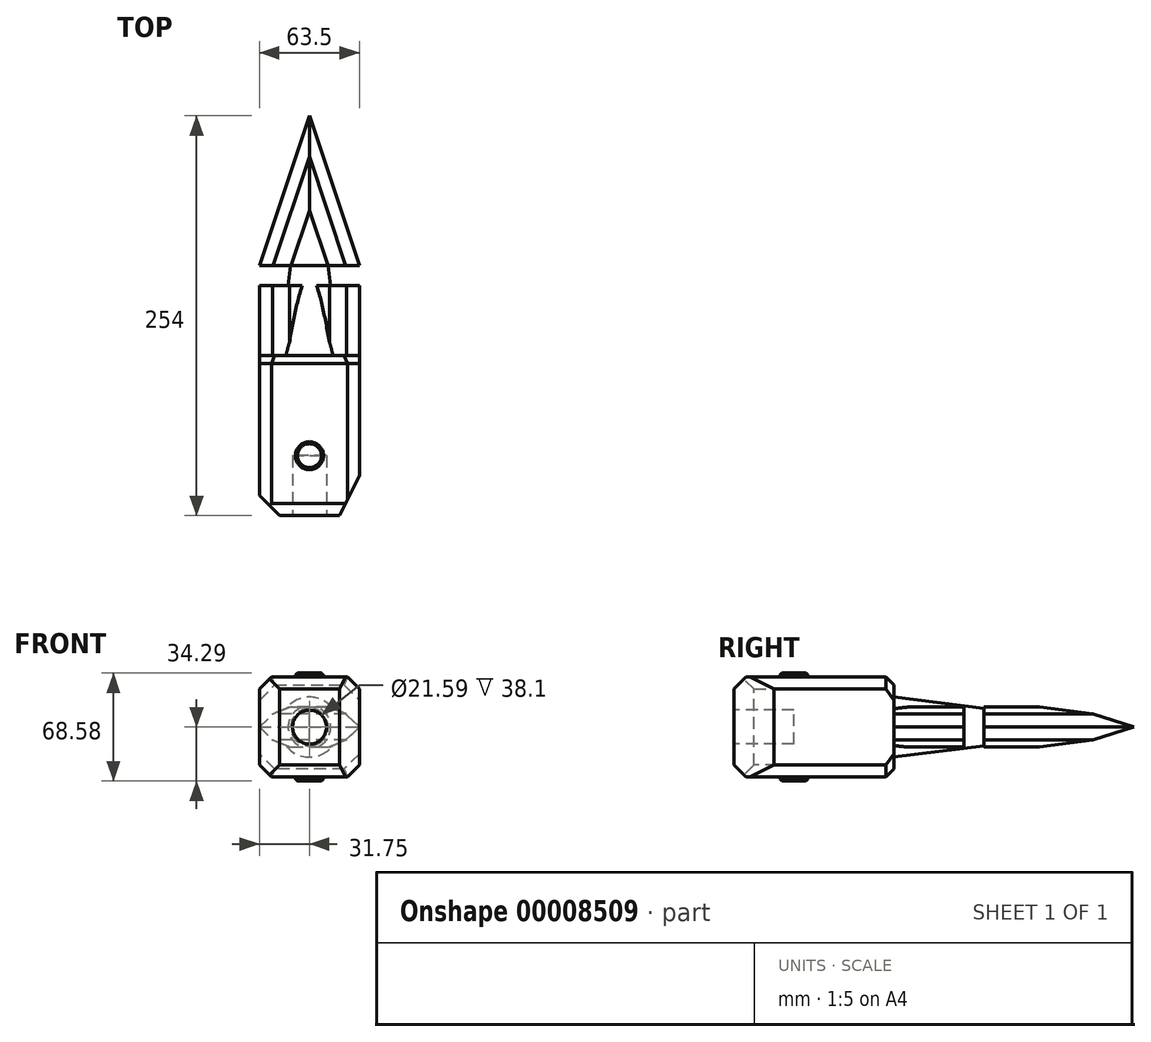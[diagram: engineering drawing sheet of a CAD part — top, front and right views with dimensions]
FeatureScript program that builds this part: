
annotation { "Feature Type Name" : "Feature", "Feature Type Description" : "" }
export const myFeature = defineFeature(function(context is Context, id is Id, definition is map)
    precondition{}
    {
        {
            var Q0;
            Q0=qCreatedBy(makeId("Top.planeOp"),FACE);
            var sketch = newSketch(context, id + "F0", { "sketchPlane" : qUnion([Q0])});
            skLineSegment(sketch, "E0.bottom", {"start": v(-31.75, -50.8) * mm, "end": v(31.75, -50.8) * mm});
            skLineSegment(sketch, "E0.top", {"start": v(-31.75, 50.8) * mm, "end": v(31.75, 50.8) * mm});
            skLineSegment(sketch, "E0.left", {"start": v(-31.75, -50.8) * mm, "end": v(-31.75, 50.8) * mm});
            skLineSegment(sketch, "E0.right", {"start": v(31.75, -50.8) * mm, "end": v(31.75, 50.8) * mm});
            skSolve(sketch);
        }
        {
            var Q0;
            Q0=makeQuery(id+"F0.imprint","IMPRINT",FACE,{"disambiguationData":[TD([[makeQuery(id+"F0.imprint","IMPRINT",EDGE,{"derivedFrom":sQuery(id+"F0.wireOp",EDGE,"E0.bottom")}),1.0]])]});
            extrude(context, id + "F1", {"entities" : qUnion([Q0]), "depth" : 63.5 * mm});
        }
        {
            var Q0;
            Q0=makeQuery(id+"F1.opExtrude","SWEPT_FACE",FACE,{"disambiguationData":[OSD([sQuery(id+"F0.wireOp",EDGE,"E0.bottom")])]});
            var sketch = newSketch(context, id + "F2", { "sketchPlane" : qUnion([Q0])});
            skLineSegment(sketch, "E1", {"start": v(0, 0) * mm, "end": v(0, 63.5) * mm, "construction": true});
            skLineSegment(sketch, "E2", {"start": v(-31.75, 31.75) * mm, "end": v(31.75, 31.75) * mm, "construction": true});
            skCircle(sketch, "E3", {"center": v(0, 31.75) * mm, "radius": 10.8 * mm});
            skSolve(sketch);
        }
        {
            var Q0;
            Q0=makeQuery(id+"F2.imprint","IMPRINT",FACE,{"disambiguationData":[TD([[makeQuery(id+"F2.imprint","IMPRINT",EDGE,{"derivedFrom":sQuery(id+"F2.wireOp",EDGE,"E3")}),1.0]])]});
            extrude(context, id + "F3", {"entities" : qUnion([Q0]), "operationType" : NewBodyOperationType.REMOVE, "oppositeDirection" : true, "depth" : 38.1 * mm});
        }
        {
            var Q0;
            Q0=makeQuery(id+"F1.opExtrude","CAP_FACE",FACE,{"disambiguationData":[OSD([sQuery(id+"F0.wireOp",EDGE,"E0.bottom"),sQuery(id+"F0.wireOp",EDGE,"E0.top"),sQuery(id+"F0.wireOp",EDGE,"E0.left"),sQuery(id+"F0.wireOp",EDGE,"E0.right")])],"isStart":false});
            var sketch = newSketch(context, id + "F4", { "sketchPlane" : qUnion([Q0])});
            skLineSegment(sketch, "E4.bottom", {"start": v(-31.75, -50.8) * mm, "end": v(-19.05, -50.8) * mm});
            skLineSegment(sketch, "E4.top", {"start": v(-31.75, -38.1) * mm, "end": v(-19.05, -38.1) * mm});
            skLineSegment(sketch, "E4.left", {"start": v(-31.75, -50.8) * mm, "end": v(-31.75, -38.1) * mm});
            skLineSegment(sketch, "E4.right", {"start": v(-19.05, -50.8) * mm, "end": v(-19.05, -38.1) * mm});
            skLineSegment(sketch, "E5.bottom", {"start": v(31.75, -50.8) * mm, "end": v(19.05, -50.8) * mm});
            skLineSegment(sketch, "E5.top", {"start": v(31.75, -25.4) * mm, "end": v(19.05, -25.4) * mm});
            skLineSegment(sketch, "E5.left", {"start": v(31.75, -50.8) * mm, "end": v(31.75, -25.4) * mm});
            skLineSegment(sketch, "E5.right", {"start": v(19.05, -50.8) * mm, "end": v(19.05, -25.4) * mm});
            skLineSegment(sketch, "E6", {"start": v(-31.75, -38.1) * mm, "end": v(-19.05, -50.8) * mm});
            skLineSegment(sketch, "E7", {"start": v(19.05, -50.8) * mm, "end": v(31.75, -25.4) * mm});
            skSolve(sketch);
        }
        {
            var Q0;
            Q0=makeQuery(id+"F4.imprint","IMPRINT",FACE,{"disambiguationData":[TD([[makeQuery(id+"F4.imprint","IMPRINT",EDGE,{"derivedFrom":sQuery(id+"F4.wireOp",EDGE,"E4.bottom")}),1.0]])]});
            var Q1;
            Q1=makeQuery(id+"F4.imprint","IMPRINT",FACE,{"disambiguationData":[TD([[makeQuery(id+"F4.imprint","IMPRINT",EDGE,{"derivedFrom":sQuery(id+"F4.wireOp",EDGE,"E5.bottom")}),1.0]])]});
            extrude(context, id + "F5", {"entities" : qUnion([Q0, Q1]), "operationType" : NewBodyOperationType.REMOVE, "oppositeDirection" : true, "depth" : 63.5 * mm});
        }
        {
            var Q0;
            Q0=makeQuery(id+"F1.opExtrude","CAP_EDGE",EDGE,{"disambiguationData":[OSD([sQuery(id+"F0.wireOp",EDGE,"E0.left")])],"isStart":false});
            var Q1;
            Q1=makeQuery(id+"F5.boolean.opBoolean","COPY",EDGE,{"derivedFrom":makeQuery(id+"F5.opExtrude","CAP_EDGE",EDGE,{"disambiguationData":[OSD([sQuery(id+"F4.wireOp",EDGE,"E6")])],"isStart":true})});
            var Q2;
            Q2=makeQuery(id+"F1.opExtrude","CAP_EDGE",EDGE,{"disambiguationData":[OSD([sQuery(id+"F0.wireOp",EDGE,"E0.bottom")])],"isStart":false});
            var Q3;
            Q3=makeQuery(id+"F5.boolean.opBoolean","COPY",EDGE,{"derivedFrom":makeQuery(id+"F5.opExtrude","CAP_EDGE",EDGE,{"disambiguationData":[OSD([sQuery(id+"F4.wireOp",EDGE,"E7")])],"isStart":true})});
            var Q4;
            Q4=makeQuery(id+"F1.opExtrude","CAP_EDGE",EDGE,{"disambiguationData":[OSD([sQuery(id+"F0.wireOp",EDGE,"E0.right")])],"isStart":false});
            var Q5;
            Q5=makeQuery(id+"F5.boolean.opBoolean","COPY",EDGE,{"derivedFrom":makeQuery(id+"F5.opExtrude","CAP_EDGE",EDGE,{"disambiguationData":[OSD([sQuery(id+"F4.wireOp",EDGE,"E7")])],"isStart":false})});
            var Q6;
            Q6=makeQuery(id+"F1.opExtrude","CAP_EDGE",EDGE,{"disambiguationData":[OSD([sQuery(id+"F0.wireOp",EDGE,"E0.right")])],"isStart":true});
            var Q7;
            Q7=makeQuery(id+"F1.opExtrude","CAP_EDGE",EDGE,{"disambiguationData":[OSD([sQuery(id+"F0.wireOp",EDGE,"E0.bottom")])],"isStart":true});
            var Q8;
            Q8=makeQuery(id+"F5.boolean.opBoolean","COPY",EDGE,{"derivedFrom":makeQuery(id+"F5.opExtrude","CAP_EDGE",EDGE,{"disambiguationData":[OSD([sQuery(id+"F4.wireOp",EDGE,"E6")])],"isStart":false})});
            var Q9;
            Q9=makeQuery(id+"F1.opExtrude","CAP_EDGE",EDGE,{"disambiguationData":[OSD([sQuery(id+"F0.wireOp",EDGE,"E0.left")])],"isStart":true});
            chamfer(context, id + "F6", {"entities" : qUnion([Q0, Q1, Q2, Q3, Q4, Q5, Q6, Q7, Q8, Q9]), "width" : 7.62 * mm, "tangentPropagation" : true});
        }
        {
            var Q0;
            Q0=makeQuery(id+"F1.opExtrude","CAP_FACE",FACE,{"disambiguationData":[OSD([sQuery(id+"F0.wireOp",EDGE,"E0.bottom"),sQuery(id+"F0.wireOp",EDGE,"E0.top"),sQuery(id+"F0.wireOp",EDGE,"E0.left"),sQuery(id+"F0.wireOp",EDGE,"E0.right")])],"isStart":false});
            var sketch = newSketch(context, id + "F7", { "sketchPlane" : qUnion([Q0])});
            skCircle(sketch, "E8", {"center": v(0, -12.7) * mm, "radius": 8.9 * mm});
            skSolve(sketch);
        }
        {
            var Q0;
            Q0=makeQuery(id+"F7.imprint","IMPRINT",FACE,{"disambiguationData":[TD([[makeQuery(id+"F7.imprint","IMPRINT",EDGE,{"derivedFrom":sQuery(id+"F7.wireOp",EDGE,"E8")}),1.0]])]});
            extrude(context, id + "F8", {"entities" : qUnion([Q0]), "operationType" : NewBodyOperationType.ADD, "depth" : 2.54 * mm});
        }
        {
            var Q0;
            Q0=makeQuery(id+"F8.opExtrude","CAP_EDGE",EDGE,{"disambiguationData":[OSD([sQuery(id+"F7.wireOp",EDGE,"E8")])],"isStart":false});
            chamfer(context, id + "F9", {"entities" : qUnion([Q0]), "width" : 1.27 * mm, "tangentPropagation" : true});
        }
        {
            var Q0;
            Q0=makeQuery(id+"F1.opExtrude","CAP_FACE",FACE,{"disambiguationData":[OSD([sQuery(id+"F0.wireOp",EDGE,"E0.bottom"),sQuery(id+"F0.wireOp",EDGE,"E0.top"),sQuery(id+"F0.wireOp",EDGE,"E0.left"),sQuery(id+"F0.wireOp",EDGE,"E0.right")])],"isStart":true});
            var sketch = newSketch(context, id + "F10", { "sketchPlane" : qUnion([Q0])});
            skCircle(sketch, "E9", {"center": v(0, 12.7) * mm, "radius": 8.9 * mm});
            skSolve(sketch);
        }
        {
            var Q0;
            Q0=makeQuery(id+"F10.imprint","IMPRINT",FACE,{"disambiguationData":[TD([[makeQuery(id+"F10.imprint","IMPRINT",EDGE,{"derivedFrom":sQuery(id+"F10.wireOp",EDGE,"E9")}),1.0]])]});
            extrude(context, id + "F11", {"entities" : qUnion([Q0]), "operationType" : NewBodyOperationType.ADD, "depth" : 2.54 * mm});
        }
        {
            var Q0;
            Q0=makeQuery(id+"F11.opExtrude","CAP_EDGE",EDGE,{"disambiguationData":[OSD([sQuery(id+"F10.wireOp",EDGE,"E9")])],"isStart":false});
            chamfer(context, id + "F12", {"entities" : qUnion([Q0]), "width" : 1.27 * mm, "tangentPropagation" : true});
        }
        {
            var Q0;
            Q0=qCreatedBy(makeId("Top.planeOp"),FACE);
            cPlane(context, id + "F13", {"entities" : qUnion([Q0]), "cplaneType" : CPlaneType.OFFSET, "offset" : 31.75 * mm, "width" : 152.4 * mm, "height" : 152.4 * mm});
        }
        {
            var Q0;
            Q0=qCreatedBy(id+"F13.planeOp",FACE);
            var sketch = newSketch(context, id + "F14", { "sketchPlane" : qUnion([Q0])});
            skLineSegment(sketch, "E10.0", {"start": v(-24.13, 50.8) * mm, "end": v(24.13, 50.8) * mm});
            skLineSegment(sketch, "E11", {"start": v(0, 50.8) * mm, "end": v(0, 203.2) * mm});
            skLineSegment(sketch, "E12", {"start": v(19.05, 50.8) * mm, "end": v(0, 203.2) * mm});
            skSolve(sketch);
        }
        {
            var Q0;
            {var subQ1=sQuery(id+"F14.wireOp",EDGE,"E11");Q0=makeQuery(id+"F14.imprint","IMPRINT",FACE,{"disambiguationData":[TD([[makeQuery(id+"F14.imprint","IMPRINT",EDGE,{"derivedFrom":subQ1}),-1.0]])]});}
            var Q1;
            Q1=sQuery(id+"F14.wireOp",EDGE,"E11");
            revolve(context, id + "F15", {"operationType" : NewBodyOperationType.ADD, "entities" : qUnion([Q0]), "axis" : qUnion([Q1]), "revolveType" : RevolveType.FULL});
        }
        {
            var Q0;
            Q0=qCreatedBy(id+"F13.planeOp",FACE);
            var sketch = newSketch(context, id + "F16", { "sketchPlane" : qUnion([Q0])});
            skLineSegment(sketch, "E13.0", {"start": v(-24.13, 50.8) * mm, "end": v(24.13, 50.8) * mm});
            skLineSegment(sketch, "E14.0", {"start": v(24.13, 50.8) * mm, "end": v(31.75, 50.8) * mm});
            skLineSegment(sketch, "E15.0", {"start": v(-31.75, 50.8) * mm, "end": v(-24.13, 50.8) * mm});
            skLineSegment(sketch, "E16.bottom", {"start": v(-31.75, 50.8) * mm, "end": v(31.75, 50.8) * mm});
            skLineSegment(sketch, "E16.top", {"start": v(-31.75, 203.2) * mm, "end": v(31.75, 203.2) * mm});
            skLineSegment(sketch, "E16.left", {"start": v(-31.75, 50.8) * mm, "end": v(-31.75, 203.2) * mm});
            skLineSegment(sketch, "E16.right", {"start": v(31.75, 50.8) * mm, "end": v(31.75, 203.2) * mm});
            skLineSegment(sketch, "E17.bottom", {"start": v(-31.75, 95.25) * mm, "end": v(31.75, 95.25) * mm});
            skLineSegment(sketch, "E17.top", {"start": v(-31.75, 107.95) * mm, "end": v(31.75, 107.95) * mm});
            skLineSegment(sketch, "E17.left", {"start": v(-31.75, 95.25) * mm, "end": v(-31.75, 107.95) * mm});
            skLineSegment(sketch, "E17.right", {"start": v(31.75, 95.25) * mm, "end": v(31.75, 107.95) * mm});
            skLineSegment(sketch, "E18", {"start": v(-31.75, 107.95) * mm, "end": v(0, 203.2) * mm});
            skLineSegment(sketch, "E19", {"start": v(0, 203.2) * mm, "end": v(31.75, 107.95) * mm});
            skSolve(sketch);
        }
        {
            var Q0;
            {var subQ0=sQuery(id+"F16.wireOp",EDGE,"E17.bottom");Q0=makeQuery(id+"F16.imprint","IMPRINT",FACE,{"disambiguationData":[TD([[makeQuery(id+"F16.imprint","IMPRINT",EDGE,{"derivedFrom":subQ0}),-1.0]])]});}
            var Q1;
            Q1=makeQuery(id+"F16.imprint","IMPRINT",FACE,{"disambiguationData":[TD([[makeQuery(id+"F16.imprint","IMPRINT",EDGE,{"derivedFrom":sQuery(id+"F16.wireOp",EDGE,"E17.top")}),1.0]])]});
            extrude(context, id + "F17", {"entities" : qUnion([Q0, Q1]), "operationType" : NewBodyOperationType.ADD, "depth" : 25.4 * mm, "symmetric" : true});
        }
        {
            var Q0;
            Q0=makeQuery(id+"F17.opExtrude","CAP_EDGE",EDGE,{"disambiguationData":[OSD([sQuery(id+"F16.wireOp",EDGE,"E19")])],"isStart":false});
            var Q1;
            Q1=makeQuery(id+"F17.opExtrude","CAP_EDGE",EDGE,{"disambiguationData":[OSD([sQuery(id+"F16.wireOp",EDGE,"E18")])],"isStart":false});
            var Q2;
            Q2=makeQuery(id+"F17.opExtrude","CAP_EDGE",EDGE,{"disambiguationData":[OSD([sQuery(id+"F16.wireOp",EDGE,"E19")])],"isStart":true});
            var Q3;
            Q3=makeQuery(id+"F17.opExtrude","CAP_EDGE",EDGE,{"disambiguationData":[OSD([sQuery(id+"F16.wireOp",EDGE,"E18")])],"isStart":true});
            var Q4;
            Q4=makeQuery(id+"F17.opExtrude","CAP_EDGE",EDGE,{"disambiguationData":[OSD([sQuery(id+"F16.wireOp",EDGE,"E16.left")])],"isStart":true});
            var Q5;
            Q5=makeQuery(id+"F17.opExtrude","CAP_EDGE",EDGE,{"disambiguationData":[OSD([sQuery(id+"F16.wireOp",EDGE,"E16.left")])],"isStart":false});
            var Q6;
            Q6=makeQuery(id+"F17.opExtrude","CAP_EDGE",EDGE,{"disambiguationData":[OSD([sQuery(id+"F16.wireOp",EDGE,"E16.right")])],"isStart":false});
            var Q7;
            Q7=makeQuery(id+"F17.opExtrude","CAP_EDGE",EDGE,{"disambiguationData":[OSD([sQuery(id+"F16.wireOp",EDGE,"E16.right")])],"isStart":true});
            chamfer(context, id + "F18", {"entities" : qUnion([Q0, Q1, Q2, Q3, Q4, Q5, Q6, Q7]), "width" : 12.7 * mm, "tangentPropagation" : true});
        }
        {
            var Q0;
            {var subQ0=sQuery(id+"F16.wireOp",EDGE,"E18");Q0=makeQuery(id+"F18.opChamfer","BLEND_EDGE",EDGE,{"blendedFrom":[makeQuery(id+"F17.opExtrude","CAP_EDGE",EDGE,{"disambiguationData":[OSD([subQ0])],"isStart":true}),makeQuery(id+"F17.opExtrude","CAP_FACE",FACE,{"disambiguationData":[OSD([sQuery(id+"F16.wireOp",EDGE,"E17.top"),subQ0,sQuery(id+"F16.wireOp",EDGE,"E19")])],"isStart":true})],"blendedInto":[makeQuery(id+"F17.opExtrude","CAP_FACE",FACE,{"disambiguationData":[OSD([sQuery(id+"F16.wireOp",EDGE,"E17.top"),subQ0,sQuery(id+"F16.wireOp",EDGE,"E19")])],"isStart":true})]});}
            var Q1;
            {var subQ0=sQuery(id+"F16.wireOp",EDGE,"E19");Q1=makeQuery(id+"F18.opChamfer","BLEND_EDGE",EDGE,{"blendedFrom":[makeQuery(id+"F17.opExtrude","CAP_EDGE",EDGE,{"disambiguationData":[OSD([subQ0])],"isStart":true}),makeQuery(id+"F17.opExtrude","CAP_FACE",FACE,{"disambiguationData":[OSD([sQuery(id+"F16.wireOp",EDGE,"E17.top"),sQuery(id+"F16.wireOp",EDGE,"E18"),subQ0])],"isStart":true})],"blendedInto":[makeQuery(id+"F17.opExtrude","CAP_FACE",FACE,{"disambiguationData":[OSD([sQuery(id+"F16.wireOp",EDGE,"E17.top"),sQuery(id+"F16.wireOp",EDGE,"E18"),subQ0])],"isStart":true})]});}
            chamfer(context, id + "F19", {"entities" : qUnion([Q0, Q1]), "width" : 15.24 * mm, "tangentPropagation" : true});
        }
        {
            var Q0;
            {var subQ0=sQuery(id+"F16.wireOp",EDGE,"E19");Q0=makeQuery(id+"F18.opChamfer","BLEND_EDGE",EDGE,{"blendedFrom":[makeQuery(id+"F17.opExtrude","CAP_EDGE",EDGE,{"disambiguationData":[OSD([subQ0])],"isStart":false}),makeQuery(id+"F17.opExtrude","CAP_FACE",FACE,{"disambiguationData":[OSD([sQuery(id+"F16.wireOp",EDGE,"E17.top"),sQuery(id+"F16.wireOp",EDGE,"E18"),subQ0])],"isStart":false})],"blendedInto":[makeQuery(id+"F17.opExtrude","CAP_FACE",FACE,{"disambiguationData":[OSD([sQuery(id+"F16.wireOp",EDGE,"E17.top"),sQuery(id+"F16.wireOp",EDGE,"E18"),subQ0])],"isStart":false})]});}
            var Q1;
            {var subQ0=sQuery(id+"F16.wireOp",EDGE,"E18");Q1=makeQuery(id+"F18.opChamfer","BLEND_EDGE",EDGE,{"blendedFrom":[makeQuery(id+"F17.opExtrude","CAP_EDGE",EDGE,{"disambiguationData":[OSD([subQ0])],"isStart":false}),makeQuery(id+"F17.opExtrude","CAP_FACE",FACE,{"disambiguationData":[OSD([sQuery(id+"F16.wireOp",EDGE,"E17.top"),subQ0,sQuery(id+"F16.wireOp",EDGE,"E19")])],"isStart":false})],"blendedInto":[makeQuery(id+"F17.opExtrude","CAP_FACE",FACE,{"disambiguationData":[OSD([sQuery(id+"F16.wireOp",EDGE,"E17.top"),subQ0,sQuery(id+"F16.wireOp",EDGE,"E19")])],"isStart":false})]});}
            chamfer(context, id + "F20", {"entities" : qUnion([Q0, Q1]), "width" : 15.24 * mm, "tangentPropagation" : true});
        }
        {
            var Q0;
            {var subQ0=sQuery(id+"F16.wireOp",EDGE,"E16.left");var subQ1=sQuery(id+"F16.wireOp",EDGE,"E17.bottom");Q0=makeQuery(id+"F18.opChamfer","BLEND_EDGE",EDGE,{"blendedFrom":[makeQuery(id+"F17.opExtrude","CAP_EDGE",EDGE,{"disambiguationData":[OSD([subQ0])],"isStart":true}),makeQuery(id+"F17.boolean.opBoolean","SPLIT",FACE,{"disambiguationData":[TD([makeQuery(id+"F1.opExtrude","SWEPT_FACE",FACE,{"disambiguationData":[OSD([sQuery(id+"F0.wireOp",EDGE,"E0.left")])]})])],"derivedFrom":makeQuery(id+"F17.opExtrude","CAP_FACE",FACE,{"disambiguationData":[OSD([sQuery(id+"F16.wireOp",EDGE,"E16.bottom"),subQ0,sQuery(id+"F16.wireOp",EDGE,"E16.right"),subQ1])],"isStart":true})})],"blendedInto":[makeQuery(id+"F17.boolean.opBoolean","SPLIT",FACE,{"disambiguationData":[TD([makeQuery(id+"F1.opExtrude","SWEPT_FACE",FACE,{"disambiguationData":[OSD([sQuery(id+"F0.wireOp",EDGE,"E0.left")])]})])],"derivedFrom":makeQuery(id+"F17.opExtrude","CAP_FACE",FACE,{"disambiguationData":[OSD([sQuery(id+"F16.wireOp",EDGE,"E16.bottom"),subQ0,sQuery(id+"F16.wireOp",EDGE,"E16.right"),subQ1])],"isStart":true})})]});}
            var Q1;
            {var subQ0=sQuery(id+"F16.wireOp",EDGE,"E16.left");var subQ1=sQuery(id+"F16.wireOp",EDGE,"E17.bottom");Q1=makeQuery(id+"F18.opChamfer","BLEND_EDGE",EDGE,{"blendedFrom":[makeQuery(id+"F17.opExtrude","CAP_EDGE",EDGE,{"disambiguationData":[OSD([subQ0])],"isStart":false}),makeQuery(id+"F17.boolean.opBoolean","SPLIT",FACE,{"disambiguationData":[TD([makeQuery(id+"F1.opExtrude","SWEPT_FACE",FACE,{"disambiguationData":[OSD([sQuery(id+"F0.wireOp",EDGE,"E0.left")])]})])],"derivedFrom":makeQuery(id+"F17.opExtrude","CAP_FACE",FACE,{"disambiguationData":[OSD([sQuery(id+"F16.wireOp",EDGE,"E16.bottom"),subQ0,sQuery(id+"F16.wireOp",EDGE,"E16.right"),subQ1])],"isStart":false})})],"blendedInto":[makeQuery(id+"F17.boolean.opBoolean","SPLIT",FACE,{"disambiguationData":[TD([makeQuery(id+"F1.opExtrude","SWEPT_FACE",FACE,{"disambiguationData":[OSD([sQuery(id+"F0.wireOp",EDGE,"E0.left")])]})])],"derivedFrom":makeQuery(id+"F17.opExtrude","CAP_FACE",FACE,{"disambiguationData":[OSD([sQuery(id+"F16.wireOp",EDGE,"E16.bottom"),subQ0,sQuery(id+"F16.wireOp",EDGE,"E16.right"),subQ1])],"isStart":false})})]});}
            var Q2;
            {var subQ0=sQuery(id+"F16.wireOp",EDGE,"E16.right");var subQ1=sQuery(id+"F16.wireOp",EDGE,"E17.bottom");Q2=makeQuery(id+"F18.opChamfer","BLEND_EDGE",EDGE,{"blendedFrom":[makeQuery(id+"F17.opExtrude","CAP_EDGE",EDGE,{"disambiguationData":[OSD([subQ0])],"isStart":true}),makeQuery(id+"F17.boolean.opBoolean","SPLIT",FACE,{"disambiguationData":[TD([makeQuery(id+"F1.opExtrude","SWEPT_FACE",FACE,{"disambiguationData":[OSD([sQuery(id+"F0.wireOp",EDGE,"E0.right")])]})])],"derivedFrom":makeQuery(id+"F17.opExtrude","CAP_FACE",FACE,{"disambiguationData":[OSD([sQuery(id+"F16.wireOp",EDGE,"E16.bottom"),sQuery(id+"F16.wireOp",EDGE,"E16.left"),subQ0,subQ1])],"isStart":true})})],"blendedInto":[makeQuery(id+"F17.boolean.opBoolean","SPLIT",FACE,{"disambiguationData":[TD([makeQuery(id+"F1.opExtrude","SWEPT_FACE",FACE,{"disambiguationData":[OSD([sQuery(id+"F0.wireOp",EDGE,"E0.right")])]})])],"derivedFrom":makeQuery(id+"F17.opExtrude","CAP_FACE",FACE,{"disambiguationData":[OSD([sQuery(id+"F16.wireOp",EDGE,"E16.bottom"),sQuery(id+"F16.wireOp",EDGE,"E16.left"),subQ0,subQ1])],"isStart":true})})]});}
            var Q3;
            {var subQ0=sQuery(id+"F16.wireOp",EDGE,"E16.right");var subQ1=sQuery(id+"F16.wireOp",EDGE,"E17.bottom");Q3=makeQuery(id+"F18.opChamfer","BLEND_EDGE",EDGE,{"blendedFrom":[makeQuery(id+"F17.opExtrude","CAP_EDGE",EDGE,{"disambiguationData":[OSD([subQ0])],"isStart":false}),makeQuery(id+"F17.boolean.opBoolean","SPLIT",FACE,{"disambiguationData":[TD([makeQuery(id+"F1.opExtrude","SWEPT_FACE",FACE,{"disambiguationData":[OSD([sQuery(id+"F0.wireOp",EDGE,"E0.right")])]})])],"derivedFrom":makeQuery(id+"F17.opExtrude","CAP_FACE",FACE,{"disambiguationData":[OSD([sQuery(id+"F16.wireOp",EDGE,"E16.bottom"),sQuery(id+"F16.wireOp",EDGE,"E16.left"),subQ0,subQ1])],"isStart":false})})],"blendedInto":[makeQuery(id+"F17.boolean.opBoolean","SPLIT",FACE,{"disambiguationData":[TD([makeQuery(id+"F1.opExtrude","SWEPT_FACE",FACE,{"disambiguationData":[OSD([sQuery(id+"F0.wireOp",EDGE,"E0.right")])]})])],"derivedFrom":makeQuery(id+"F17.opExtrude","CAP_FACE",FACE,{"disambiguationData":[OSD([sQuery(id+"F16.wireOp",EDGE,"E16.bottom"),sQuery(id+"F16.wireOp",EDGE,"E16.left"),subQ0,subQ1])],"isStart":false})})]});}
            chamfer(context, id + "F21", {"entities" : qUnion([Q0, Q1, Q2, Q3]), "width" : 15.24 * mm, "tangentPropagation" : true});
        }
        {
            var Q0;
            Q0=makeQuery(id+"F1.opExtrude","CAP_EDGE",EDGE,{"disambiguationData":[OSD([sQuery(id+"F0.wireOp",EDGE,"E0.top")])],"isStart":false});
            var Q1;
            Q1=makeQuery(id+"F6.opChamfer","BLEND_EDGE",EDGE,{"blendedFrom":[makeQuery(id+"F1.opExtrude","CAP_EDGE",EDGE,{"disambiguationData":[OSD([sQuery(id+"F0.wireOp",EDGE,"E0.right")])],"isStart":false}),makeQuery(id+"F1.opExtrude","SWEPT_FACE",FACE,{"disambiguationData":[OSD([sQuery(id+"F0.wireOp",EDGE,"E0.top")])]})],"blendedInto":[makeQuery(id+"F1.opExtrude","SWEPT_FACE",FACE,{"disambiguationData":[OSD([sQuery(id+"F0.wireOp",EDGE,"E0.top")])]})]});
            var Q2;
            Q2=makeQuery(id+"F6.opChamfer","BLEND_EDGE",EDGE,{"blendedFrom":[makeQuery(id+"F1.opExtrude","CAP_EDGE",EDGE,{"disambiguationData":[OSD([sQuery(id+"F0.wireOp",EDGE,"E0.left")])],"isStart":false}),makeQuery(id+"F1.opExtrude","SWEPT_FACE",FACE,{"disambiguationData":[OSD([sQuery(id+"F0.wireOp",EDGE,"E0.top")])]})],"blendedInto":[makeQuery(id+"F1.opExtrude","SWEPT_FACE",FACE,{"disambiguationData":[OSD([sQuery(id+"F0.wireOp",EDGE,"E0.top")])]})]});
            var Q3;
            Q3=makeQuery(id+"F6.opChamfer","BLEND_EDGE",EDGE,{"blendedFrom":[makeQuery(id+"F1.opExtrude","CAP_EDGE",EDGE,{"disambiguationData":[OSD([sQuery(id+"F0.wireOp",EDGE,"E0.right")])],"isStart":true}),makeQuery(id+"F1.opExtrude","SWEPT_FACE",FACE,{"disambiguationData":[OSD([sQuery(id+"F0.wireOp",EDGE,"E0.top")])]})],"blendedInto":[makeQuery(id+"F1.opExtrude","SWEPT_FACE",FACE,{"disambiguationData":[OSD([sQuery(id+"F0.wireOp",EDGE,"E0.top")])]})]});
            var Q4;
            Q4=makeQuery(id+"F6.opChamfer","BLEND_EDGE",EDGE,{"blendedFrom":[makeQuery(id+"F1.opExtrude","CAP_EDGE",EDGE,{"disambiguationData":[OSD([sQuery(id+"F0.wireOp",EDGE,"E0.left")])],"isStart":true}),makeQuery(id+"F1.opExtrude","SWEPT_FACE",FACE,{"disambiguationData":[OSD([sQuery(id+"F0.wireOp",EDGE,"E0.top")])]})],"blendedInto":[makeQuery(id+"F1.opExtrude","SWEPT_FACE",FACE,{"disambiguationData":[OSD([sQuery(id+"F0.wireOp",EDGE,"E0.top")])]})]});
            var Q5;
            Q5=makeQuery(id+"F1.opExtrude","CAP_EDGE",EDGE,{"disambiguationData":[OSD([sQuery(id+"F0.wireOp",EDGE,"E0.top")])],"isStart":true});
            chamfer(context, id + "F22", {"entities" : qUnion([Q0, Q1, Q2, Q3, Q4, Q5]), "width" : 5.08 * mm, "tangentPropagation" : true});
        }
    });
